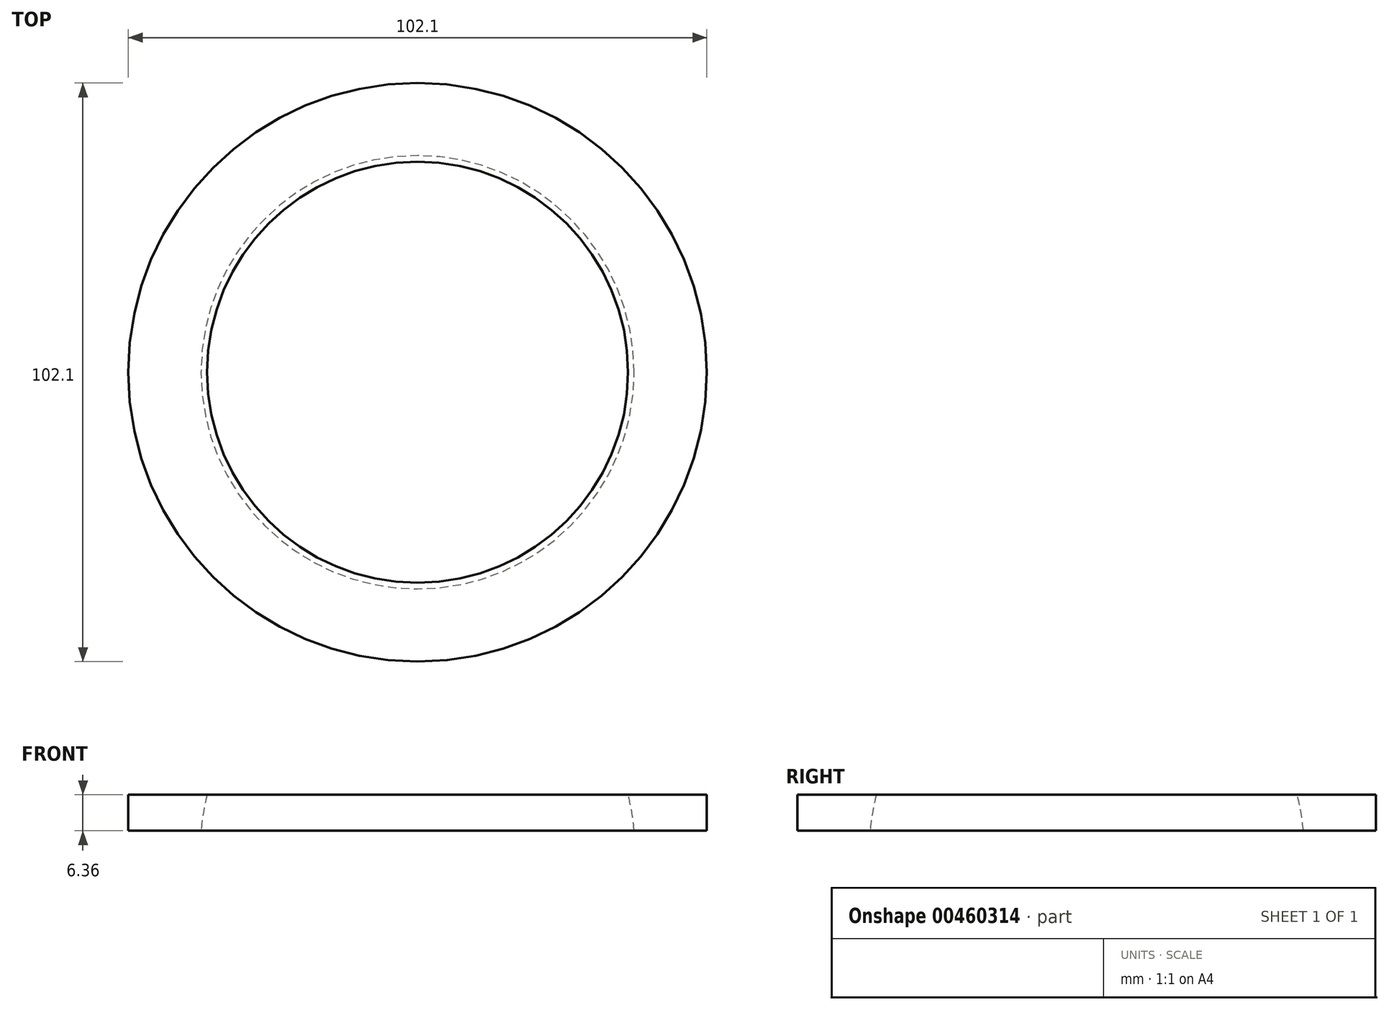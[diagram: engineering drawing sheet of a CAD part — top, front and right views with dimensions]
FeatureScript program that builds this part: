
annotation { "Feature Type Name" : "Feature", "Feature Type Description" : "" }
export const myFeature = defineFeature(function(context is Context, id is Id, definition is map)
    precondition{}
    {
        {
            var Q0;
            Q0=qCreatedBy(makeId("Front.planeOp"),FACE);
            var sketch = newSketch(context, id + "F0", { "sketchPlane" : qUnion([Q0])});
            skArc(sketch, "E0", {"start": v(38.22, 3.17) * mm, "mid": v(37.82, 6.37) * mm, "end": v(37.15, 9.52) * mm});
            skLineSegment(sketch, "E1.bottom", {"start": v(37.15, 9.53) * mm, "end": v(51.05, 9.53) * mm});
            skLineSegment(sketch, "E1.top", {"start": v(38.22, 3.17) * mm, "end": v(51.05, 3.17) * mm});
            skLineSegment(sketch, "E1.right", {"start": v(51.05, 9.52) * mm, "end": v(51.05, 3.18) * mm});
            skPoint(sketch, "E1.left.start.orphan", {"position": v(0, 9.52) * mm});
            skLineSegment(sketch, "E2", {"start": v(0, 34.7) * mm, "end": v(0, -31.48) * mm, "construction": true});
            skSolve(sketch);
        }
        {
            var Q0;
            Q0 = qSketchRegion(id + "F0", true);
            var Q1;
            Q1=sQuery(id+"F0.wireOp",EDGE,"E2");
            revolve(context, id + "F1", {"entities" : qUnion([Q0]), "axis" : qUnion([Q1]), "revolveType" : RevolveType.FULL});
        }
    });
